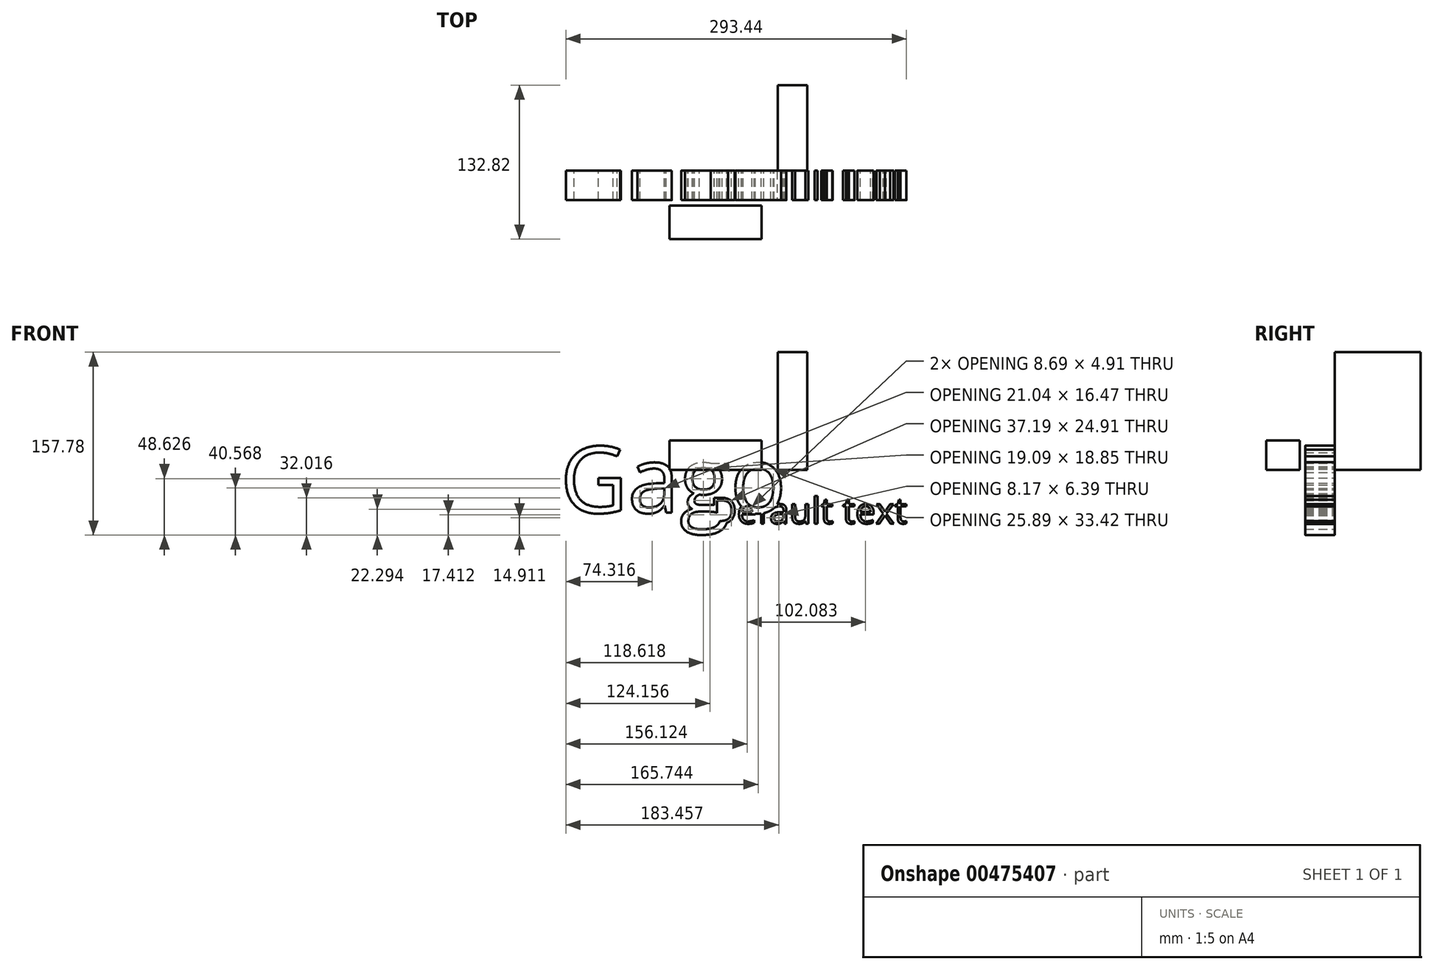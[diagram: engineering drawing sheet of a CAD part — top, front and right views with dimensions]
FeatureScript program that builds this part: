
annotation { "Feature Type Name" : "Feature", "Feature Type Description" : "" }
export const myFeature = defineFeature(function(context is Context, id is Id, definition is map)
    precondition{}
    {
        {
            var Q0;
            Q0=qCreatedBy(makeId("Top.planeOp"),FACE);
            var sketch = newSketch(context, id + "F0", { "sketchPlane" : qUnion([Q0])});
            skLineSegment(sketch, "E0", {"start": v(39.23, 73.93) * mm, "end": v(39.23, 0) * mm});
            skSolve(sketch);
        }
        {
            var Q0;
            Q0=sQuery(id+"F0.wireOp",EDGE,"E0");
            extrude(context, id + "F1", {"bodyType" : ToolBodyType.SURFACE, "surfaceEntities" : qUnion([Q0]), "depth" : 101.6 * mm});
        }
        {
            var Q0;
            Q0=makeQuery(id+"F1.opExtrude","SWEPT_FACE",FACE,{"disambiguationData":[OSD([sQuery(id+"F0.wireOp",EDGE,"E0")])]});
            extrude(context, id + "F2", {"entities" : qUnion([Q0]), "depth" : 25.4 * mm});
        }
        {
            var Q0;
            Q0=qCreatedBy(makeId("Top.planeOp"),FACE);
            var sketch = newSketch(context, id + "F3", { "sketchPlane" : qUnion([Q0])});
            skLineSegment(sketch, "E1.bottom", {"start": v(0, -58.89) * mm, "end": v(-79.56, -58.89) * mm});
            skLineSegment(sketch, "E1.top", {"start": v(0, -30.1) * mm, "end": v(-79.56, -30.1) * mm});
            skLineSegment(sketch, "E1.left", {"start": v(0, -58.89) * mm, "end": v(0, -30.1) * mm});
            skLineSegment(sketch, "E1.right", {"start": v(-79.56, -58.89) * mm, "end": v(-79.56, -30.1) * mm});
            skSolve(sketch);
        }
        {
            var Q0;
            Q0=makeQuery(id+"F3.imprint","IMPRINT",FACE,{"disambiguationData":[TD([[makeQuery(id+"F3.imprint","IMPRINT",EDGE,{"derivedFrom":sQuery(id+"F3.wireOp",EDGE,"E1.bottom")}),-1.0]])]});
            var sketch = newSketch(context, id + "F4", { "sketchPlane" : qUnion([Q0])});
            skSolve(sketch);
        }
        {
            var Q0;
            Q0 = qSketchRegion(id + "F4", true);
            var Q1;
            Q1=makeQuery(id+"F4.imprint","IMPRINT",FACE,{"disambiguationData":[TD([[makeQuery(id+"F4.imprint","IMPRINT",EDGE,{"derivedFrom":makeQuery(id+"F3.imprint","IMPRINT",EDGE,{"derivedFrom":sQuery(id+"F3.wireOp",EDGE,"E1.bottom")})}),-1.0]])]});
            extrude(context, id + "F5", {"entities" : qUnion([Q0, Q1]), "depth" : 25.4 * mm});
        }
        {
            var Q0;
            Q0=qCreatedBy(makeId("Front.planeOp"),FACE);
            var sketch = newSketch(context, id + "F6", { "sketchPlane" : qUnion([Q0])});
            skText(sketch, "E2", { "text": "Gago", "fontName": "OpenSans-Regular.ttf"});
            skText(sketch, "E3", { "text": "Default text", "fontName": "OpenSans-Regular.ttf"});
            const initialGuessF6  = {"E2": [-0.17357, -0.03697, 1, 0, 0.05757], "E3": [-0.04395, -0.04624, 1, 0, 0.02235]};
            skSetInitialGuess(sketch, initialGuessF6);
            skSolve(sketch);
        }
        {
            var Q0;
            Q0 = qSketchRegion(id + "F6", true);
            extrude(context, id + "F7", {"entities" : qUnion([Q0]), "depth" : 25.4 * mm});
        }
    });
